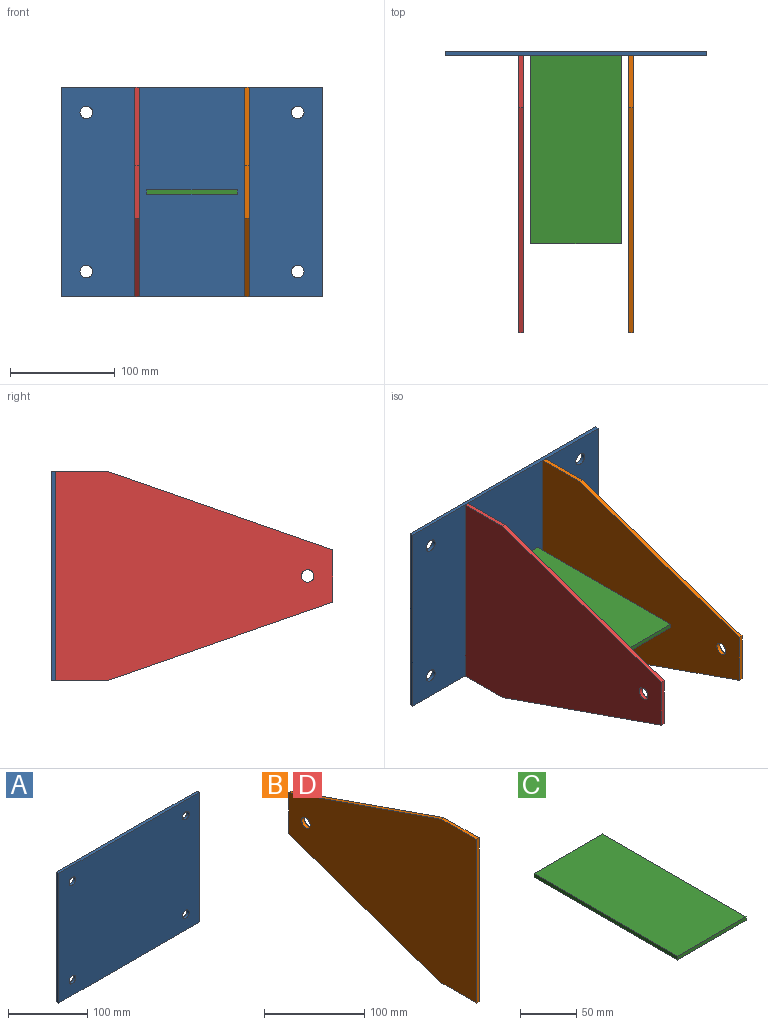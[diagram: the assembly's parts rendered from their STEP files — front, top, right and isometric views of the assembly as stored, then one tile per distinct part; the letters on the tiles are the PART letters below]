
ASSEMBLY  parts=4 mates=5
PART A: 10 faces, bbox 250x4x200 mm
  f0: plane 200x4mm, normal (-1,0,0), area 800mm2, adj f1,f6,f8,f9
  f1: plane 250x4mm, normal (0,0,-1), area 1000mm2, adj f0,f2,f8,f9
  f2: plane 200x4mm, normal (1,0,0), area 800mm2, adj f1,f6,f8,f9
  f3: cylinder r=6mm len=12mm, axis (0,1,0), area 150.8mm2, adj f8,f9
  f4: cylinder r=6mm len=12mm, axis (0,1,0), area 150.8mm2, adj f8,f9
  f5: cylinder r=6mm len=12mm, axis (0,1,0), area 150.8mm2, adj f8,f9
  f6: plane 250x4mm, normal (0,0,1), area 1000mm2, adj f0,f2,f8,f9
  f7: cylinder r=6mm len=12mm, axis (0,1,0), area 150.8mm2, adj f8,f9
  f8: plane 250x200mm, normal (0,-1,0), area 49547.6mm2, adj f0,f1,f2,f3,f4,f5,f6,f7
  f9: plane 250x200mm, normal (0,1,0), area 49547.6mm2, adj f0,f1,f2,f3,f4,f5,f6,f7
PART B: 9 faces, bbox 4x265x200 mm
  f0: plane 50x4mm, normal (0,0,1), area 200mm2, adj f1,f5,f7,f8
  f1: plane 200x4mm, normal (0,-1,0), area 800mm2, adj f0,f2,f7,f8
  f2: plane 50x4mm, normal (0,0,-1), area 200mm2, adj f1,f3,f7,f8
  f3: plane 215x75mm, normal (0,0.33,-0.94), area 910.8mm2, adj f2,f4,f7,f8
  f4: plane 50x4mm, normal (0,1,0), area 200mm2, adj f3,f5,f7,f8
  f5: plane 215x75mm, normal (0,0.33,0.94), area 910.8mm2, adj f0,f4,f7,f8
  f6: cylinder r=6mm len=12mm, axis (-1,0,0), area 150.8mm2, adj f7,f8
  f7: plane 265x200mm, normal (1,0,0), area 36761.9mm2, adj f0,f1,f2,f3,f4,f5,f6
  f8: plane 265x200mm, normal (-1,0,0), area 36761.9mm2, adj f0,f1,f2,f3,f4,f5,f6
PART C: 6 faces, bbox 86x180x4 mm
  f0: plane 86x4mm, normal (0,1,0), area 344mm2, adj f1,f3,f4,f5
  f1: plane 180x4mm, normal (-1,0,0), area 720mm2, adj f0,f2,f4,f5
  f2: plane 86x4mm, normal (0,-1,0), area 344mm2, adj f1,f3,f4,f5
  f3: plane 180x4mm, normal (1,0,0), area 720mm2, adj f0,f2,f4,f5
  f4: plane 180x86mm, normal (0,0,1), area 15480mm2, adj f0,f1,f2,f3
  f5: plane 180x86mm, normal (0,0,-1), area 15480mm2, adj f0,f1,f2,f3
PART D: same geometry as B
PLACE A t=(-135.44,161.32,-234.99)mm
PLACE B rot(axis=(1,0,0),180deg) t=(40.06,157.32,-34.99)mm
PLACE C rot(axis=(0,0,1),0deg) t=(-53.44,157.32,-136.99)mm
PLACE D rot(axis=(1,0,0),180deg) t=(-64.94,157.32,-34.99)mm
MATE planar C.f0 <-> A.f8  axis (0,1,0) through (-10.44,157.32,-134.99)mm
MATE planar D.f2 <-> A.f6  axis (0,0,1) through (-62.94,132.32,-34.99)mm
MATE planar B.f2 <-> A.f6  axis (0,0,1) through (42.06,132.32,-34.99)mm
MATE planar D.f1 <-> A.f8  axis (0,1,0) through (-62.94,157.32,-134.99)mm
MATE planar B.f1 <-> C.f0  axis (0,1,0) through (42.06,157.32,-134.99)mm
